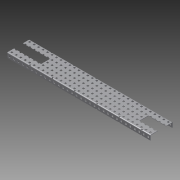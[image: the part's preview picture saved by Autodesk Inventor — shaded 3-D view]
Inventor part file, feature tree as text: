
AUTODESK INVENTOR PART (.ipt)
format: ipt  version: 2012 (Build 160160000, 160)  size: 3,072,000 bytes
history: native  units: in
note: dims shown in document units (in); Inventor stores cm internally (conversion verified against a paired STEP export)
features: extrude x3, sketch x3, plane x2, other x1, imported_body x1, split x1
ambient origin geometry x8: Origin, YZ Plane, XZ Plane, XY Plane, X Axis, Y Axis, Z Axis, Center Point
feature tree (11):
  parser-record x1  (decoder bookkeeping rows leaked as tree rows — omitted from the tree; the rows remain in map.json)
  imported_body  "Base1"
  plane  "Work Plane1"
  plane  "Work Plane3"
  split  "Split3"
  extrude  "Extrusion1"  [1 undecoded]
  extrude  "Extrusion2"  Depth=1.0in TaperAngle=0.0deg
  extrude  "Extrusion3"  [1 undecoded]
  sketch  "Sketch1"  dims[d0=-0.5in d2=-1.5in]
  sketch  "Sketch2"  dims[d3=1.0in d4=0.0in d5=1.0in d6=0.0in]
  sketch  "Sketch3"  dims[d7=1.0in d8=0.0in]
note: 2 required parameter values undecoded (feature->parameter linkage not recoverable at this tier; creation-order binding heuristic only, values carry confidence <= 0.55)
